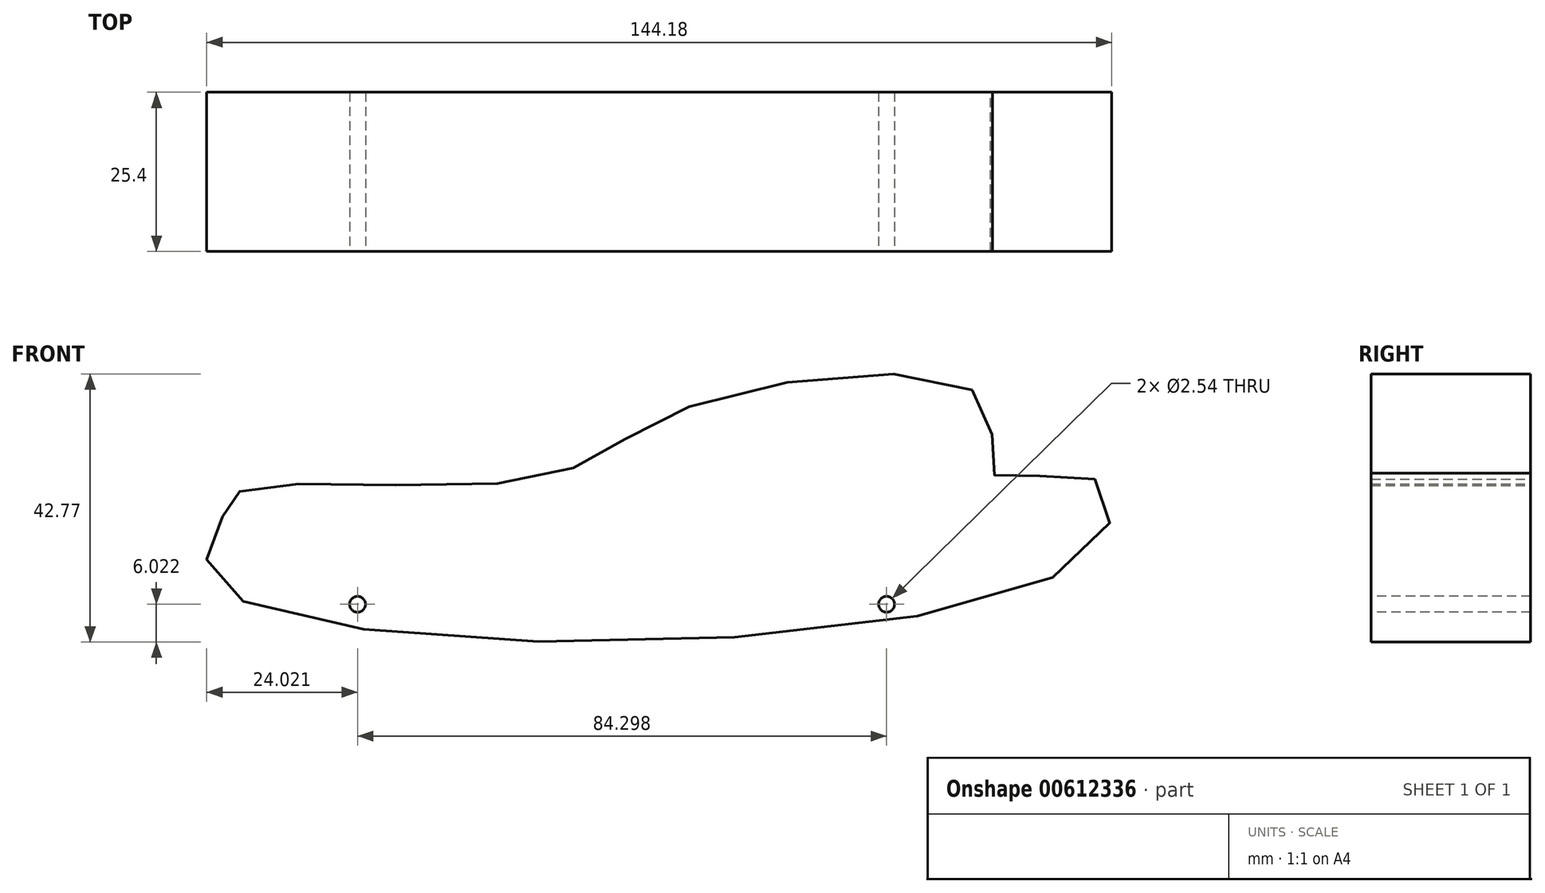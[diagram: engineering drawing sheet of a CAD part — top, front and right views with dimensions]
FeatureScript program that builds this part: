
annotation { "Feature Type Name" : "Feature", "Feature Type Description" : "" }
export const myFeature = defineFeature(function(context is Context, id is Id, definition is map)
    precondition{}
    {
        {
            var Q0;
            Q0=qCreatedBy(makeId("Front.planeOp"),FACE);
            var sketch = newSketch(context, id + "F0", { "sketchPlane" : qUnion([Q0])});
            skFitSpline(sketch, "E0", {"points": [v(-64.57, 0) * mm, v(-60.9, 4.41) * mm, v(-14.1, 6.13) * mm, v(9.43, 17.4) * mm, v(56.97, 18.38) * mm, v(58.45, 6.62) * mm, v(73.64, 6.37) * mm, v(72.17, -7.1) * mm, v(-65.06, -11.27) * mm, v(-64.57, 0) * mm]});
            skSolve(sketch);
        }
        {
            var Q0;
            Q0=makeQuery(id+"F0.imprint","IMPRINT",FACE,{"disambiguationData":[TD([[makeQuery(id+"F0.imprint","IMPRINT",EDGE,{"derivedFrom":sQuery(id+"F0.wireOp",EDGE,"E0")}),-1.0]])]});
            extrude(context, id + "F1", {"entities" : qUnion([Q0]), "depth" : 25.4 * mm, "offsetDistance" : 25.4 * mm});
        }
        {
            var Q0;
            Q0=makeQuery(id+"F1.opExtrude","CAP_FACE",FACE,{"disambiguationData":[OSD([sQuery(id+"F0.wireOp",EDGE,"E0")])],"isStart":false});
            var sketch = newSketch(context, id + "F2", { "sketchPlane" : qUnion([Q0])});
            skCircle(sketch, "E1", {"center": v(41.26, -13.97) * mm, "radius": 1.27 * mm});
            skCircle(sketch, "E2", {"center": v(-43.04, -13.97) * mm, "radius": 1.27 * mm});
            skSolve(sketch);
        }
        {
            var Q0;
            Q0=sQuery(id+"F2.wireOp",VERTEX,"E2.center");
            var Q1;
            Q1=sQuery(id+"F2.wireOp",VERTEX,"E1.center");
            var Q2;
            Q2=makeQuery(id+"F1.opExtrude","SWEPT_BODY",BODY,{"disambiguationData":[OSD([sQuery(id+"F0.wireOp",EDGE,"E0")])]});
            hole(context, id + "F3", {"style" : HoleStyle.SIMPLE, "endStyle" : HoleEndStyle.THROUGH, "holeDiameter" : 2.54 * mm, "majorDiameter" : 6.35 * mm, "isTappedThrough" : true, "tappedDepth" : 12.7 * mm, "tapClearance" : 3, "locations" : qUnion([Q0, Q1]), "scope" : qUnion([Q2])});
        }
    });
